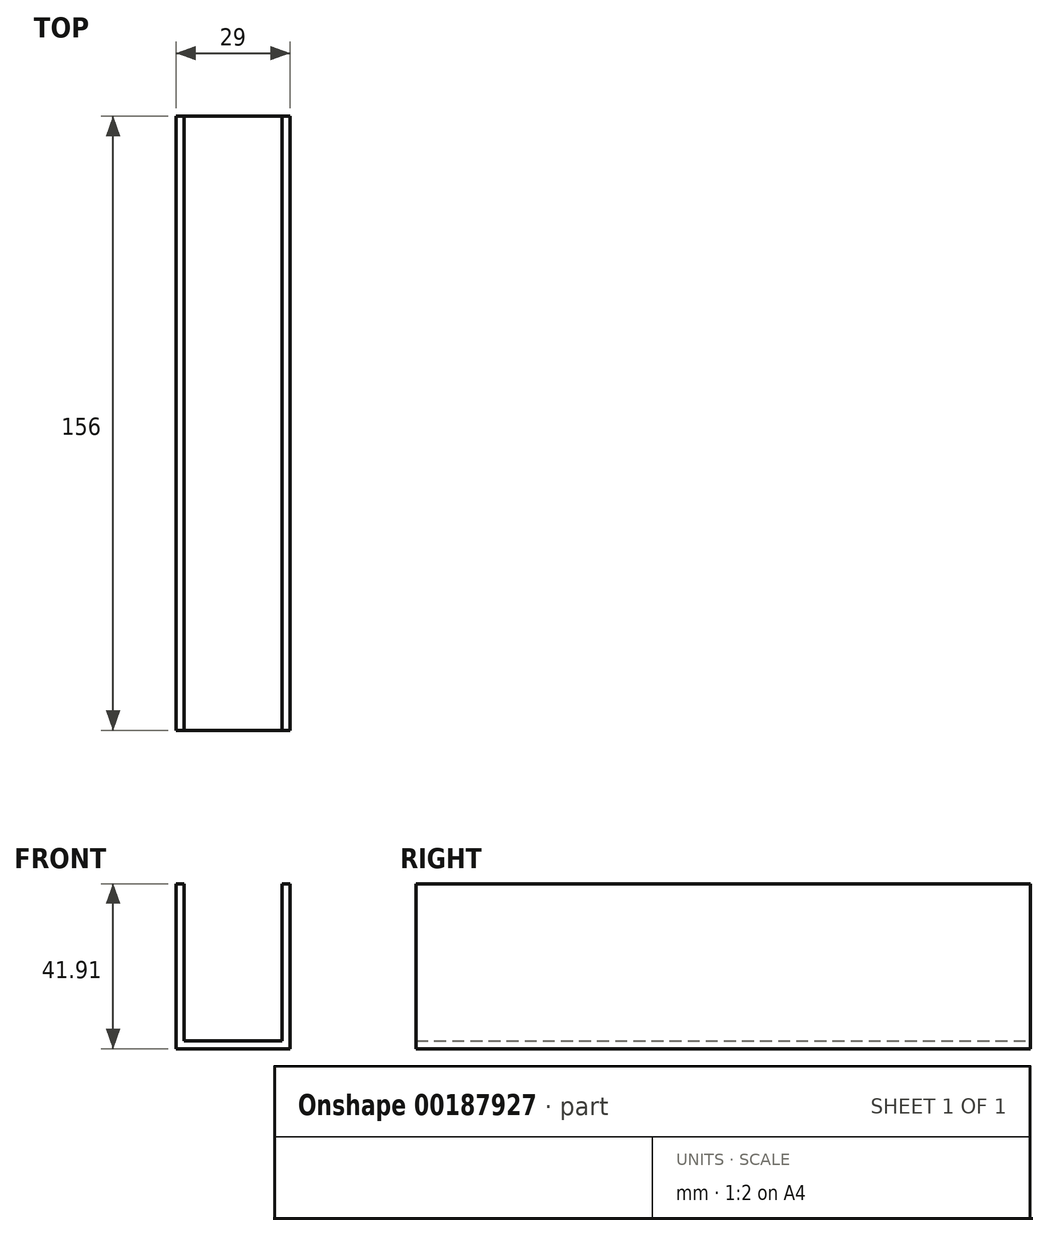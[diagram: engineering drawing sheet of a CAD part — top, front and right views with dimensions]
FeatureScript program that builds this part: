
annotation { "Feature Type Name" : "Feature", "Feature Type Description" : "" }
export const myFeature = defineFeature(function(context is Context, id is Id, definition is map)
    precondition{}
    {
        {
            var Q0;
            Q0=qCreatedBy(makeId("Front.planeOp"),FACE);
            var sketch = newSketch(context, id + "F0", { "sketchPlane" : qUnion([Q0])});
            skLineSegment(sketch, "E0", {"start": v(0, 0) * mm, "end": v(0, 41.9) * mm});
            skLineSegment(sketch, "E1", {"start": v(0, 41.9) * mm, "end": v(29, 41.9) * mm});
            skLineSegment(sketch, "E2", {"start": v(29, 41.9) * mm, "end": v(29, 0) * mm});
            skLineSegment(sketch, "E3", {"start": v(29, 0) * mm, "end": v(0, 0) * mm});
            skSolve(sketch);
        }
        {
            var Q0;
            Q0=makeQuery(id+"F0.imprint","IMPRINT",FACE,{"disambiguationData":[TD([[makeQuery(id+"F0.imprint","IMPRINT",EDGE,{"derivedFrom":sQuery(id+"F0.wireOp",EDGE,"E0")}),-1.0]])]});
            extrude(context, id + "F1", {"entities" : qUnion([Q0]), "depth" : 156 * mm});
        }
        {
            var Q0;
            Q0=makeQuery(id+"F1.opExtrude","CAP_FACE",FACE,{"disambiguationData":[OSD([sQuery(id+"F0.wireOp",EDGE,"E0"),sQuery(id+"F0.wireOp",EDGE,"E1"),sQuery(id+"F0.wireOp",EDGE,"E2"),sQuery(id+"F0.wireOp",EDGE,"E3")])],"isStart":true});
            var sketch = newSketch(context, id + "F2", { "sketchPlane" : qUnion([Q0])});
            skLineSegment(sketch, "E4", {"start": v(-26.97, 41.9) * mm, "end": v(-2.08, 41.9) * mm});
            skLineSegment(sketch, "E5", {"start": v(-2.08, 41.9) * mm, "end": v(-2.08, 2.03) * mm});
            skLineSegment(sketch, "E6", {"start": v(-2.08, 2.03) * mm, "end": v(-26.97, 2.03) * mm});
            skLineSegment(sketch, "E7", {"start": v(-26.97, 2.03) * mm, "end": v(-26.97, 41.9) * mm});
            skSolve(sketch);
        }
        {
            var Q0;
            Q0=makeQuery(id+"F2.imprint","IMPRINT",FACE,{"disambiguationData":[TD([[makeQuery(id+"F2.imprint","IMPRINT",EDGE,{"derivedFrom":sQuery(id+"F2.wireOp",EDGE,"E4")}),1.0]])]});
            extrude(context, id + "F3", {"entities" : qUnion([Q0]), "operationType" : NewBodyOperationType.REMOVE, "endBound" : BoundingType.THROUGH_ALL, "oppositeDirection" : true, "depth" : 25.4 * mm});
        }
    });
